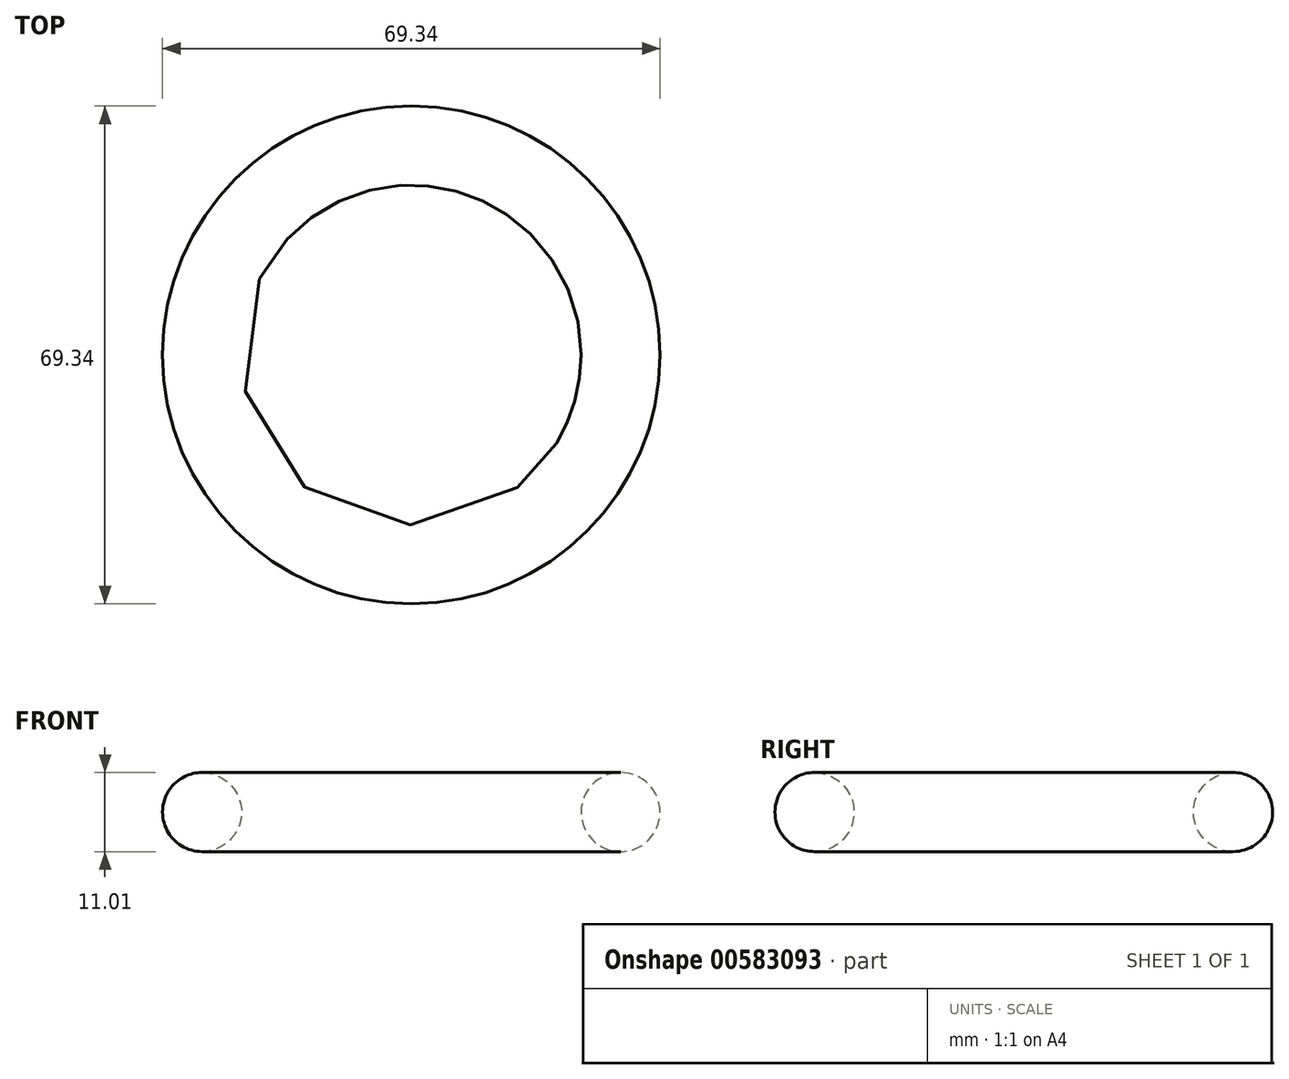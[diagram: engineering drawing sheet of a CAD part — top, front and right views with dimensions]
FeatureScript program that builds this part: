
annotation { "Feature Type Name" : "Feature", "Feature Type Description" : "" }
export const myFeature = defineFeature(function(context is Context, id is Id, definition is map)
    precondition{}
    {
        {
            var Q0;
            Q0=qCreatedBy(makeId("Front.planeOp"),FACE);
            var sketch = newSketch(context, id + "F0", { "sketchPlane" : qUnion([Q0])});
            skLineSegment(sketch, "E0", {"start": v(0, 57.29) * mm, "end": v(0, -52.55) * mm, "construction": true});
            skCircle(sketch, "E1", {"center": v(51.96, 24.72) * mm, "radius": 12.32 * mm, "construction": true});
            skCircle(sketch, "E2", {"center": v(29.16, -22.94) * mm, "radius": 5.5 * mm});
            skSolve(sketch);
        }
        {
            var Q0;
            Q0 = qSketchRegion(id + "F0", true);
            var Q1;
            Q1=sQuery(id+"F0.wireOp",EDGE,"E0");
            revolve(context, id + "F1", {"entities" : qUnion([Q0]), "axis" : qUnion([Q1]), "revolveType" : RevolveType.FULL});
        }
    });
